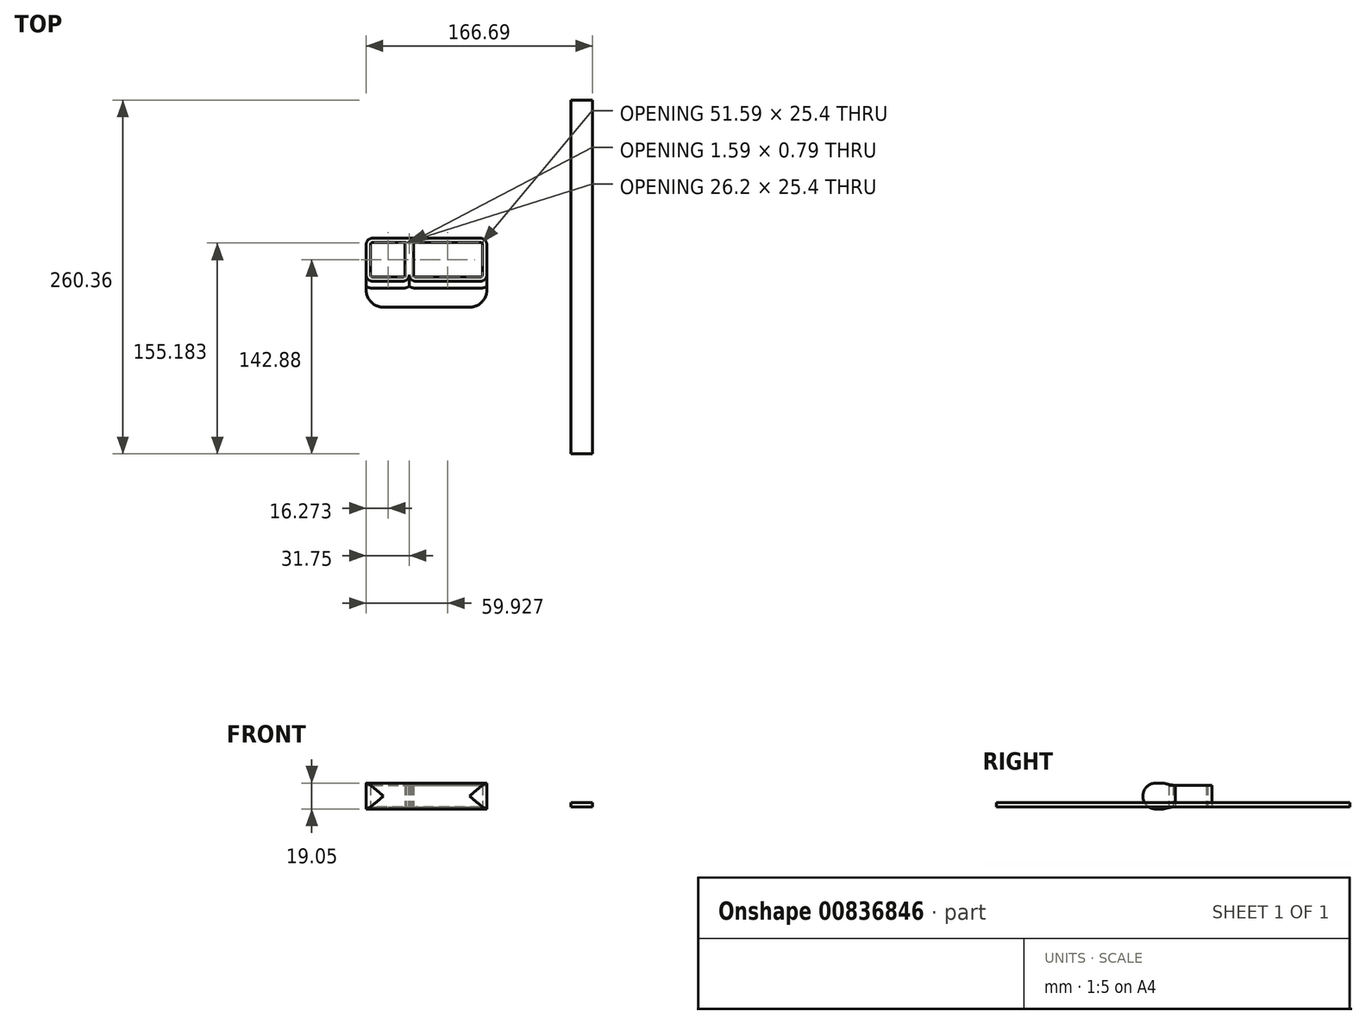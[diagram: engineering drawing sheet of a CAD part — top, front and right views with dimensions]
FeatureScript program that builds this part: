
annotation { "Feature Type Name" : "Feature", "Feature Type Description" : "" }
export const myFeature = defineFeature(function(context is Context, id is Id, definition is map)
    precondition{}
    {
        {
            var Q0;
            Q0=qCreatedBy(makeId("Top.planeOp"),FACE);
            var sketch = newSketch(context, id + "F0", { "sketchPlane" : qUnion([Q0])});
            skLineSegment(sketch, "E0.bottom", {"start": v(-26.99, 0) * mm, "end": v(-4.76, 0) * mm});
            skLineSegment(sketch, "E0.top", {"start": v(-26.99, 25.4) * mm, "end": v(52.39, 25.4) * mm});
            skLineSegment(sketch, "E0.left", {"start": v(-28.57, 1.59) * mm, "end": v(-28.58, 23.81) * mm});
            skLineSegment(sketch, "E0.right", {"start": v(53.98, 1.59) * mm, "end": v(53.98, 23.81) * mm});
            skLineSegment(sketch, "E1", {"start": v(-3.18, 24.6) * mm, "end": v(-3.17, 1.59) * mm});
            skLineSegment(sketch, "E2", {"start": v(3.17, 24.6) * mm, "end": v(3.18, 1.59) * mm});
            skLineSegment(sketch, "E3.bottom", {"start": v(-26.99, 28.57) * mm, "end": v(52.39, 28.58) * mm});
            skLineSegment(sketch, "E3.top", {"start": v(4.76, -3.18) * mm, "end": v(52.39, -3.17) * mm});
            skLineSegment(sketch, "E3.left", {"start": v(-31.75, 23.81) * mm, "end": v(-31.75, 1.59) * mm});
            skLineSegment(sketch, "E3.right", {"start": v(57.15, 23.81) * mm, "end": v(57.15, 1.59) * mm});
            skLineSegment(sketch, "E4", {"start": v(0, 24.6) * mm, "end": v(0, 1.59) * mm});
            skLineSegment(sketch, "E5.trimOffspring", {"start": v(4.76, 0) * mm, "end": v(52.39, 0) * mm});
            skArc(sketch, "E6", {"start": v(-2.38, 25.4) * mm, "mid": v(-2.94, 25.17) * mm, "end": v(-3.18, 24.6) * mm});
            skArc(sketch, "E7", {"start": v(0, 24.6) * mm, "mid": v(-0.23, 25.17) * mm, "end": v(-0.8, 25.4) * mm});
            skPoint(sketch, "E8.orphan", {"position": v(0, 25.4) * mm});
            skArc(sketch, "E9", {"start": v(0, 24.6) * mm, "mid": v(0.23, 25.17) * mm, "end": v(0.8, 25.4) * mm});
            skArc(sketch, "E10", {"start": v(3.17, 24.6) * mm, "mid": v(2.94, 25.17) * mm, "end": v(2.38, 25.4) * mm});
            skPoint(sketch, "E11.orphan", {"position": v(3.17, 25.4) * mm});
            skArc(sketch, "E12.filletArc", {"start": v(0, 1.59) * mm, "mid": v(1.4, -1.78) * mm, "end": v(4.76, -3.18) * mm});
            skLineSegment(sketch, "E13", {"start": v(-26.99, -3.18) * mm, "end": v(-4.76, -3.18) * mm});
            skLineSegment(sketch, "E14", {"start": v(0, 1.59) * mm, "end": v(0, 1.59) * mm});
            skPoint(sketch, "E15.visualSharp", {"position": v(0, -3.18) * mm});
            skArc(sketch, "E15.filletArc", {"start": v(-4.76, -3.18) * mm, "mid": v(-1.4, -1.78) * mm, "end": v(0, 1.59) * mm});
            skPoint(sketch, "E16.visualSharp", {"position": v(-31.75, -3.18) * mm});
            skArc(sketch, "E16.filletArc", {"start": v(-31.75, 1.59) * mm, "mid": v(-30.36, -1.78) * mm, "end": v(-26.99, -3.18) * mm});
            skPoint(sketch, "E17.visualSharp", {"position": v(-31.75, 28.57) * mm});
            skArc(sketch, "E17.filletArc", {"start": v(-26.99, 28.57) * mm, "mid": v(-30.36, 27.18) * mm, "end": v(-31.75, 23.81) * mm});
            skPoint(sketch, "E18.visualSharp", {"position": v(57.15, 28.58) * mm});
            skArc(sketch, "E18.filletArc", {"start": v(57.15, 23.81) * mm, "mid": v(55.76, 27.18) * mm, "end": v(52.39, 28.58) * mm});
            skPoint(sketch, "E19.visualSharp", {"position": v(57.15, -3.17) * mm});
            skArc(sketch, "E19.filletArc", {"start": v(52.39, -3.17) * mm, "mid": v(55.76, -1.78) * mm, "end": v(57.15, 1.59) * mm});
            skPoint(sketch, "E20.visualSharp", {"position": v(-3.17, 0) * mm});
            skArc(sketch, "E20.filletArc", {"start": v(-4.76, 0) * mm, "mid": v(-3.64, 0.46) * mm, "end": v(-3.17, 1.59) * mm});
            skPoint(sketch, "E21.visualSharp", {"position": v(3.18, 0) * mm});
            skArc(sketch, "E21.filletArc", {"start": v(3.18, 1.59) * mm, "mid": v(3.64, 0.46) * mm, "end": v(4.76, 0) * mm});
            skPoint(sketch, "E22.visualSharp", {"position": v(53.98, 0) * mm});
            skArc(sketch, "E22.filletArc", {"start": v(52.39, 0) * mm, "mid": v(53.51, 0.46) * mm, "end": v(53.98, 1.59) * mm});
            skPoint(sketch, "E23.visualSharp", {"position": v(53.98, 25.4) * mm});
            skArc(sketch, "E23.filletArc", {"start": v(53.98, 23.81) * mm, "mid": v(53.51, 24.94) * mm, "end": v(52.39, 25.4) * mm});
            skPoint(sketch, "E24.visualSharp", {"position": v(-28.58, 25.4) * mm});
            skArc(sketch, "E24.filletArc", {"start": v(-26.99, 25.4) * mm, "mid": v(-28.11, 24.94) * mm, "end": v(-28.58, 23.81) * mm});
            skPoint(sketch, "E25.visualSharp", {"position": v(-28.57, 0) * mm});
            skArc(sketch, "E25.filletArc", {"start": v(-28.58, 1.59) * mm, "mid": v(-28.11, 0.46) * mm, "end": v(-26.99, 0) * mm});
            skLineSegment(sketch, "E26.bottom", {"start": v(-31.75, -3.18) * mm, "end": v(57.15, -3.18) * mm});
            skLineSegment(sketch, "E26.top", {"start": v(-19.05, -22.23) * mm, "end": v(44.45, -22.23) * mm});
            skLineSegment(sketch, "E26.left", {"start": v(-31.75, -3.18) * mm, "end": v(-31.75, -9.53) * mm});
            skLineSegment(sketch, "E26.right", {"start": v(57.15, -3.18) * mm, "end": v(57.15, -9.53) * mm});
            skLineSegment(sketch, "E27", {"start": v(-31.75, 1.59) * mm, "end": v(-31.75, -3.18) * mm});
            skLineSegment(sketch, "E28", {"start": v(57.15, 1.59) * mm, "end": v(57.15, -3.17) * mm});
            skPoint(sketch, "E29.visualSharp", {"position": v(-31.75, -22.23) * mm});
            skArc(sketch, "E29.filletArc", {"start": v(-31.75, -9.53) * mm, "mid": v(-28.03, -18.5) * mm, "end": v(-19.05, -22.23) * mm});
            skPoint(sketch, "E30.visualSharp", {"position": v(57.15, -22.23) * mm});
            skArc(sketch, "E30.filletArc", {"start": v(44.45, -22.23) * mm, "mid": v(53.43, -18.5) * mm, "end": v(57.15, -9.53) * mm});
            skSolve(sketch);
        }
        {
            var Q0;
            Q0=makeQuery(id+"F0.imprint","IMPRINT",FACE,{"disambiguationData":[TD([[makeQuery(id+"F0.imprint","IMPRINT",EDGE,{"derivedFrom":sQuery(id+"F0.wireOp",EDGE,"E0.bottom")}),-1.0]])]});
            extrude(context, id + "F1", {"entities" : qUnion([Q0]), "depth" : 15.88 * mm, "offsetDistance" : 25.4 * mm});
        }
        {
            var Q0;
            Q0=sQuery(id+"F0.wireOp",EDGE,"E4");
            extrude(context, id + "F2", {"bodyType" : ToolBodyType.SURFACE, "surfaceEntities" : qUnion([Q0]), "depth" : 15.88 * mm, "offsetDistance" : 25.4 * mm});
        }
        {
            var Q0;
            Q0=makeQuery(id+"F0.imprint","IMPRINT",FACE,{"disambiguationData":[TD([[makeQuery(id+"F0.imprint","IMPRINT",EDGE,{"derivedFrom":sQuery(id+"F0.wireOp",EDGE,"E26.top")}),1.0]])]});
            var Q1;
            {var subQ0=sQuery(id+"F0.wireOp",EDGE,"E12.filletArc");Q1=makeQuery(id+"F0.imprint","IMPRINT",FACE,{"disambiguationData":[TD([[makeQuery(id+"F0.imprint","IMPRINT",EDGE,{"derivedFrom":subQ0}),-1.0]])]});}
            var Q2;
            {var subQ0=sQuery(id+"F0.wireOp",EDGE,"E19.filletArc");Q2=makeQuery(id+"F0.imprint","IMPRINT",FACE,{"disambiguationData":[TD([[makeQuery(id+"F0.imprint","IMPRINT",EDGE,{"derivedFrom":subQ0}),-1.0]])]});}
            var Q3;
            {var subQ0=sQuery(id+"F0.wireOp",EDGE,"E16.filletArc");Q3=makeQuery(id+"F0.imprint","IMPRINT",FACE,{"disambiguationData":[TD([[makeQuery(id+"F0.imprint","IMPRINT",EDGE,{"derivedFrom":subQ0}),-1.0]])]});}
            extrude(context, id + "F3", {"entities" : qUnion([Q0, Q1, Q2, Q3]), "depth" : 17.46 * mm, "offsetDistance" : 25.4 * mm, "hasSecondDirection" : true, "secondDirectionOppositeDirection" : true, "secondDirectionDepth" : 1.59 * mm});
        }
        {
            var Q0;
            Q0=makeQuery(id+"F3.opExtrude","CAP_EDGE",EDGE,{"disambiguationData":[OSD([sQuery(id+"F0.wireOp",EDGE,"E16.filletArc")])],"isStart":false});
            var Q1;
            {var subQ0=sQuery(id+"F0.wireOp",EDGE,"E26.bottom");Q1=makeQuery(id+"F3.opExtrude","CAP_EDGE",EDGE,{"disambiguationData":[OSD([subQ0]),TDD([makeQuery(id+"F0.imprint","IMPRINT",EDGE,{"disambiguationData":[TD([[makeQuery(id+"F0.imprint","INTERSECT",VERTEX,{"derivedFrom":[sQuery(id+"F0.wireOp",EDGE,"E15.filletArc"),subQ0]}),1.0]])],"derivedFrom":subQ0})])],"isStart":false});}
            var Q2;
            Q2=makeQuery(id+"F3.opExtrude","CAP_EDGE",EDGE,{"disambiguationData":[OSD([sQuery(id+"F0.wireOp",EDGE,"E12.filletArc")])],"isStart":false});
            var Q3;
            {var subQ0=sQuery(id+"F0.wireOp",EDGE,"E26.bottom");Q3=makeQuery(id+"F3.opExtrude","CAP_EDGE",EDGE,{"disambiguationData":[OSD([subQ0]),TDD([makeQuery(id+"F0.imprint","IMPRINT",EDGE,{"disambiguationData":[TD([[makeQuery(id+"F0.imprint","INTERSECT",VERTEX,{"derivedFrom":[sQuery(id+"F0.wireOp",EDGE,"E12.filletArc"),subQ0]}),-1.0]])],"derivedFrom":subQ0})])],"isStart":false});}
            var Q4;
            Q4=makeQuery(id+"F3.opExtrude","CAP_EDGE",EDGE,{"disambiguationData":[OSD([sQuery(id+"F0.wireOp",EDGE,"E15.filletArc")])],"isStart":false});
            var Q5;
            Q5=makeQuery(id+"F3.opExtrude","CAP_EDGE",EDGE,{"disambiguationData":[OSD([sQuery(id+"F0.wireOp",EDGE,"E19.filletArc")])],"isStart":false});
            chamfer(context, id + "F4", {"entities" : qUnion([Q0, Q1, Q2, Q3, Q4, Q5]), "chamferType" : ChamferType.TWO_OFFSETS, "width1" : 1.59 * mm, "oppositeDirection" : false, "width2" : 5.08 * mm, "tangentPropagation" : true});
        }
        {
            var Q0;
            Q0=makeQuery(id+"F3.opExtrude","CAP_EDGE",EDGE,{"disambiguationData":[OSD([sQuery(id+"F0.wireOp",EDGE,"E19.filletArc")])],"isStart":true});
            var Q1;
            {var subQ0=sQuery(id+"F0.wireOp",EDGE,"E26.bottom");Q1=makeQuery(id+"F3.opExtrude","CAP_EDGE",EDGE,{"disambiguationData":[OSD([subQ0]),TDD([makeQuery(id+"F0.imprint","IMPRINT",EDGE,{"disambiguationData":[TD([[makeQuery(id+"F0.imprint","INTERSECT",VERTEX,{"derivedFrom":[sQuery(id+"F0.wireOp",EDGE,"E12.filletArc"),subQ0]}),-1.0]])],"derivedFrom":subQ0})])],"isStart":true});}
            var Q2;
            Q2=makeQuery(id+"F3.opExtrude","CAP_EDGE",EDGE,{"disambiguationData":[OSD([sQuery(id+"F0.wireOp",EDGE,"E12.filletArc")])],"isStart":true});
            var Q3;
            Q3=makeQuery(id+"F3.opExtrude","CAP_EDGE",EDGE,{"disambiguationData":[OSD([sQuery(id+"F0.wireOp",EDGE,"E15.filletArc")])],"isStart":true});
            var Q4;
            {var subQ0=sQuery(id+"F0.wireOp",EDGE,"E26.bottom");Q4=makeQuery(id+"F3.opExtrude","CAP_EDGE",EDGE,{"disambiguationData":[OSD([subQ0]),TDD([makeQuery(id+"F0.imprint","IMPRINT",EDGE,{"disambiguationData":[TD([[makeQuery(id+"F0.imprint","INTERSECT",VERTEX,{"derivedFrom":[sQuery(id+"F0.wireOp",EDGE,"E15.filletArc"),subQ0]}),1.0]])],"derivedFrom":subQ0})])],"isStart":true});}
            var Q5;
            Q5=makeQuery(id+"F3.opExtrude","CAP_EDGE",EDGE,{"disambiguationData":[OSD([sQuery(id+"F0.wireOp",EDGE,"E16.filletArc")])],"isStart":true});
            chamfer(context, id + "F5", {"entities" : qUnion([Q0, Q1, Q2, Q3, Q4, Q5]), "chamferType" : ChamferType.TWO_OFFSETS, "width1" : 5.08 * mm, "oppositeDirection" : false, "width2" : 1.59 * mm, "tangentPropagation" : true});
        }
        {
            var Q0;
            Q0=makeQuery(id+"F3.opExtrude","SWEPT_FACE",FACE,{"disambiguationData":[OSD([sQuery(id+"F0.wireOp",EDGE,"E26.top")])]});
            fillet(context, id + "F6", {"entities" : qUnion([Q0]), "radius" : 9.52 * mm, "allowEdgeOverflow" : false});
        }
        {
            var Q0;
            Q0=qCreatedBy(makeId("Top.planeOp"),FACE);
            var sketch = newSketch(context, id + "F7", { "sketchPlane" : qUnion([Q0])});
            skLineSegment(sketch, "E31.bottom", {"start": v(134.94, -130.17) * mm, "end": v(119.06, -130.17) * mm});
            skLineSegment(sketch, "E31.top", {"start": v(134.94, 130.18) * mm, "end": v(119.06, 130.18) * mm});
            skLineSegment(sketch, "E31.left", {"start": v(134.94, -130.17) * mm, "end": v(134.94, 130.18) * mm});
            skLineSegment(sketch, "E31.right", {"start": v(119.06, -130.17) * mm, "end": v(119.06, 130.18) * mm});
            skPoint(sketch, "E31.middle", {"position": v(127, 0) * mm});
            skLineSegment(sketch, "E32", {"start": v(119.06, -104.77) * mm, "end": v(134.94, -104.77) * mm});
            skLineSegment(sketch, "E33", {"start": v(119.06, -79.37) * mm, "end": v(134.94, -79.37) * mm});
            skLineSegment(sketch, "E34", {"start": v(119.06, -53.97) * mm, "end": v(134.94, -53.97) * mm});
            skLineSegment(sketch, "E35", {"start": v(119.06, 28.58) * mm, "end": v(134.94, 28.58) * mm});
            skLineSegment(sketch, "E36", {"start": v(119.06, 53.98) * mm, "end": v(134.94, 53.98) * mm});
            skLineSegment(sketch, "E37", {"start": v(119.06, 104.78) * mm, "end": v(134.94, 104.78) * mm});
            skSolve(sketch);
        }
        {
            var Q0;
            Q0 = qSketchRegion(id + "F7", true);
            extrude(context, id + "F8", {"entities" : qUnion([Q0]), "depth" : 3.17 * mm, "offsetDistance" : 25.4 * mm});
        }
        {
            var Q0;
            Q0=sQuery(id+"F7.wireOp",EDGE,"E32");
            var Q1;
            Q1=sQuery(id+"F7.wireOp",EDGE,"E33");
            var Q2;
            Q2=sQuery(id+"F7.wireOp",EDGE,"E34");
            var Q3;
            Q3=sQuery(id+"F7.wireOp",EDGE,"E35");
            var Q4;
            Q4=sQuery(id+"F7.wireOp",EDGE,"E36");
            var Q5;
            Q5=sQuery(id+"F7.wireOp",EDGE,"E37");
            extrude(context, id + "F9", {"bodyType" : ToolBodyType.SURFACE, "surfaceEntities" : qUnion([Q0, Q1, Q2, Q3, Q4, Q5]), "depth" : 3.17 * mm, "offsetDistance" : 25.4 * mm});
        }
    });
